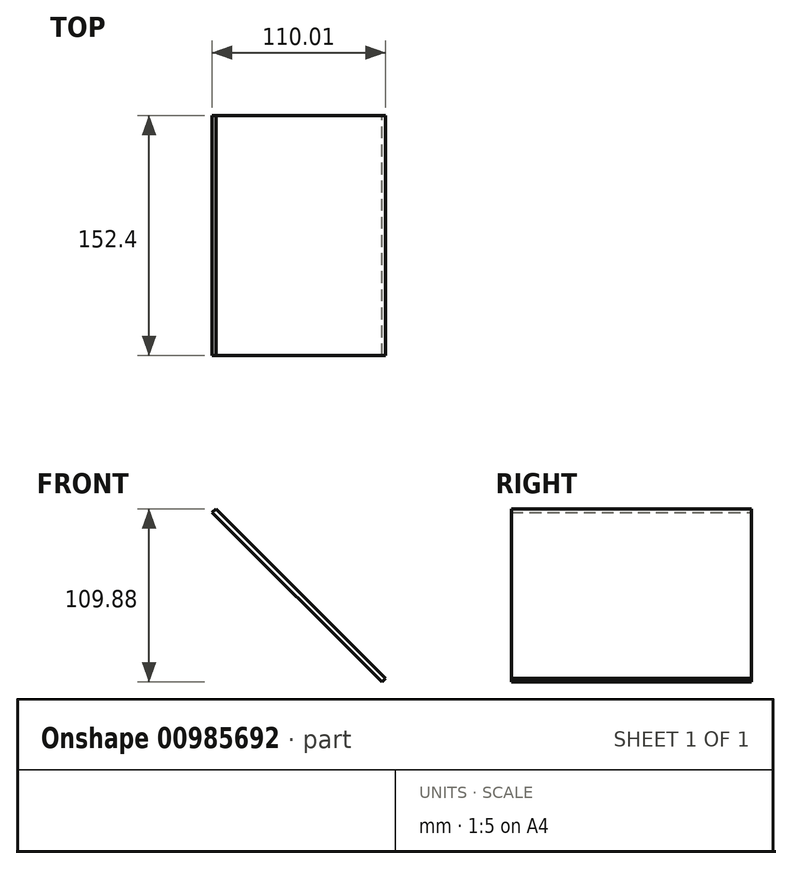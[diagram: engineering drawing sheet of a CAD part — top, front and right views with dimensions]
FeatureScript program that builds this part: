
annotation { "Feature Type Name" : "Feature", "Feature Type Description" : "" }
export const myFeature = defineFeature(function(context is Context, id is Id, definition is map)
    precondition{}
    {
        {
            var Q0;
            Q0=qCreatedBy(makeId("Front.planeOp"),FACE);
            var sketch = newSketch(context, id + "F0", { "sketchPlane" : qUnion([Q0])});
            skLineSegment(sketch, "E0", {"start": v(0, 0) * mm, "end": v(-107.76, 107.76) * mm});
            skLineSegment(sketch, "E1.0", {"start": v(2.25, 2.25) * mm, "end": v(-105.4, 109.88) * mm});
            skLineSegment(sketch, "E2", {"start": v(-107.76, 107.76) * mm, "end": v(-105.4, 109.88) * mm});
            skLineSegment(sketch, "E3", {"start": v(0, 0) * mm, "end": v(2.25, 2.25) * mm});
            skLineSegment(sketch, "E4", {"start": v(0, 0) * mm, "end": v(70.54, 0) * mm, "construction": true});
            skSolve(sketch);
        }
        {
            var Q0;
            Q0=makeQuery(id+"F0.imprint","IMPRINT",FACE,{"disambiguationData":[TD([[makeQuery(id+"F0.imprint","IMPRINT",EDGE,{"derivedFrom":sQuery(id+"F0.wireOp",EDGE,"E0")}),-1.0]])]});
            extrude(context, id + "F1", {"entities" : qUnion([Q0]), "depth" : 152.4 * mm, "offsetDistance" : 25.4 * mm});
        }
    });
